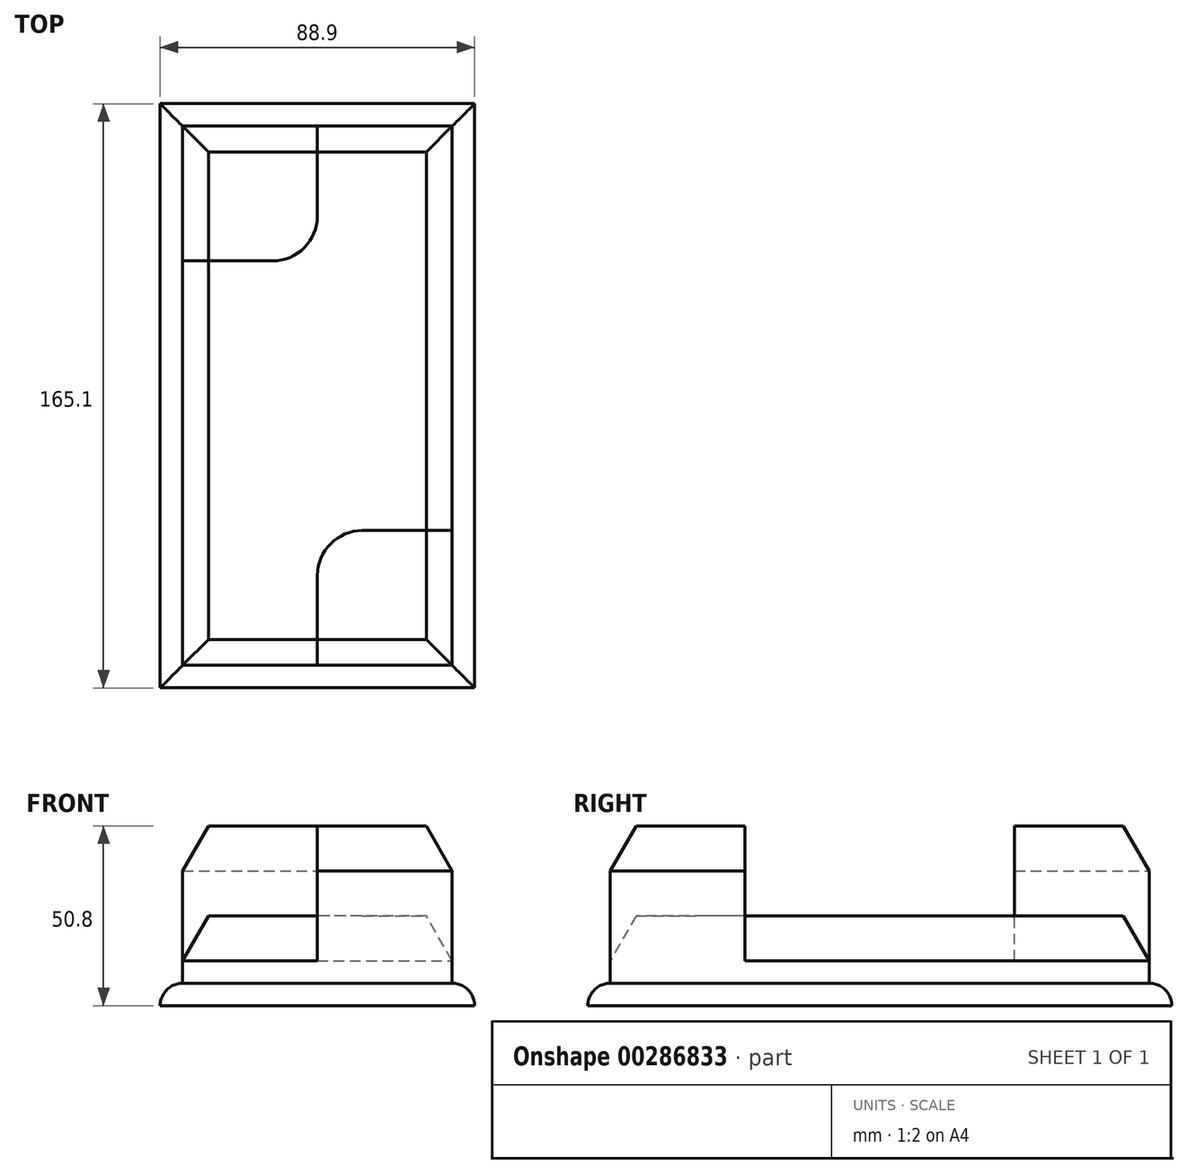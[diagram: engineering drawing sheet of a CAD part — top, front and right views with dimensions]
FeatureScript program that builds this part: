
annotation { "Feature Type Name" : "Feature", "Feature Type Description" : "" }
export const myFeature = defineFeature(function(context is Context, id is Id, definition is map)
    precondition{}
    {
        {
            var Q0;
            Q0=qCreatedBy(makeId("Top.planeOp"),FACE);
            var sketch = newSketch(context, id + "F0", { "sketchPlane" : qUnion([Q0])});
            skLineSegment(sketch, "E0", {"start": v(-43.8, 68.26) * mm, "end": v(-43.8, -84.14) * mm});
            skLineSegment(sketch, "E1", {"start": v(-43.8, -84.14) * mm, "end": v(32.4, -84.14) * mm});
            skLineSegment(sketch, "E2", {"start": v(32.4, -84.14) * mm, "end": v(32.4, 68.26) * mm});
            skLineSegment(sketch, "E3", {"start": v(32.4, 68.26) * mm, "end": v(-43.8, 68.26) * mm});
            skLineSegment(sketch, "E4", {"start": v(-5.7, 68.26) * mm, "end": v(-5.7, 42.86) * mm});
            skLineSegment(sketch, "E5", {"start": v(-18.4, 30.16) * mm, "end": v(-43.8, 30.16) * mm});
            skPoint(sketch, "E6.visualSharp", {"position": v(-5.7, 30.16) * mm});
            skArc(sketch, "E6.filletArc", {"start": v(-18.4, 30.16) * mm, "mid": v(-9.43, 33.88) * mm, "end": v(-5.7, 42.86) * mm});
            skLineSegment(sketch, "E7.0", {"start": v(38.74, 74.61) * mm, "end": v(-50.16, 74.61) * mm});
            skLineSegment(sketch, "E7.1", {"start": v(38.74, -90.49) * mm, "end": v(38.74, 74.61) * mm});
            skLineSegment(sketch, "E7.2", {"start": v(-50.16, -90.49) * mm, "end": v(38.74, -90.49) * mm});
            skLineSegment(sketch, "E7.3", {"start": v(-50.16, 74.61) * mm, "end": v(-50.16, -90.49) * mm});
            skLineSegment(sketch, "E8", {"start": v(-5.7, -84.14) * mm, "end": v(-5.7, -58.74) * mm});
            skLineSegment(sketch, "E9", {"start": v(7, -46.04) * mm, "end": v(32.4, -46.04) * mm});
            skPoint(sketch, "E10.visualSharp", {"position": v(-5.7, -46.04) * mm});
            skArc(sketch, "E10.filletArc", {"start": v(7, -46.04) * mm, "mid": v(-1.99, -49.76) * mm, "end": v(-5.7, -58.74) * mm});
            skSolve(sketch);
        }
        {
            var Q0;
            Q0=qSketchRegion(id+"F0",true);
            extrude(context, id + "F1", {"entities" : qUnion([Q0]), "depth" : 6.35 * mm});
        }
        {
            var Q0;
            {var subQ8=sQuery(id+"F0.wireOp",EDGE,"E4");Q0=makeQuery(id+"F0.imprint","IMPRINT",FACE,{"disambiguationData":[TD([[makeQuery(id+"F0.imprint","IMPRINT",EDGE,{"derivedFrom":subQ8}),1.0]])]});}
            extrude(context, id + "F2", {"entities" : qUnion([Q0]), "operationType" : NewBodyOperationType.ADD, "depth" : 25.4 * mm});
        }
        {
            var Q0;
            {var subQ1=sQuery(id+"F0.wireOp",EDGE,"E4");Q0=makeQuery(id+"F0.imprint","IMPRINT",FACE,{"disambiguationData":[TD([[makeQuery(id+"F0.imprint","IMPRINT",EDGE,{"derivedFrom":subQ1}),-1.0]])]});}
            var Q1;
            {var subQ1=sQuery(id+"F0.wireOp",EDGE,"E8");Q1=makeQuery(id+"F0.imprint","IMPRINT",FACE,{"disambiguationData":[TD([[makeQuery(id+"F0.imprint","IMPRINT",EDGE,{"derivedFrom":subQ1}),-1.0]])]});}
            extrude(context, id + "F3", {"entities" : qUnion([Q0, Q1]), "operationType" : NewBodyOperationType.ADD, "depth" : 50.8 * mm});
        }
        {
            var Q0;
            Q0=makeQuery(id+"F2.opExtrude","CAP_EDGE",EDGE,{"disambiguationData":[OSD([sQuery(id+"F0.wireOp",EDGE,"E1")])],"isStart":false});
            var Q1;
            Q1=makeQuery(id+"F3.opExtrude","CAP_EDGE",EDGE,{"disambiguationData":[OSD([sQuery(id+"F0.wireOp",EDGE,"E1")])],"isStart":false});
            var Q2;
            Q2=makeQuery(id+"F3.opExtrude","CAP_EDGE",EDGE,{"disambiguationData":[OSD([sQuery(id+"F0.wireOp",EDGE,"E2")])],"isStart":false});
            var Q3;
            Q3=makeQuery(id+"F2.opExtrude","CAP_EDGE",EDGE,{"disambiguationData":[OSD([sQuery(id+"F0.wireOp",EDGE,"E2")])],"isStart":false});
            var Q4;
            Q4=makeQuery(id+"F2.opExtrude","CAP_EDGE",EDGE,{"disambiguationData":[OSD([sQuery(id+"F0.wireOp",EDGE,"E3")])],"isStart":false});
            var Q5;
            Q5=makeQuery(id+"F3.opExtrude","CAP_EDGE",EDGE,{"disambiguationData":[OSD([sQuery(id+"F0.wireOp",EDGE,"E3")])],"isStart":false});
            var Q6;
            Q6=makeQuery(id+"F3.opExtrude","CAP_EDGE",EDGE,{"disambiguationData":[OSD([sQuery(id+"F0.wireOp",EDGE,"E0")])],"isStart":false});
            var Q7;
            Q7=makeQuery(id+"F2.opExtrude","CAP_EDGE",EDGE,{"disambiguationData":[OSD([sQuery(id+"F0.wireOp",EDGE,"E0")])],"isStart":false});
            chamfer(context, id + "F4", {"entities" : qUnion([Q0, Q1, Q2, Q3, Q4, Q5, Q6, Q7]), "chamferType" : ChamferType.OFFSET_ANGLE, "width" : 12.7 * mm, "oppositeDirection" : true, "angle" : 30 * degree, "tangentPropagation" : true});
        }
        {
            var Q0;
            Q0=makeQuery(id+"F1.opExtrude","CAP_EDGE",EDGE,{"disambiguationData":[OSD([sQuery(id+"F0.wireOp",EDGE,"E7.1")])],"isStart":false});
            var Q1;
            Q1=makeQuery(id+"F1.opExtrude","CAP_EDGE",EDGE,{"disambiguationData":[OSD([sQuery(id+"F0.wireOp",EDGE,"E7.0")])],"isStart":false});
            var Q2;
            Q2=makeQuery(id+"F1.opExtrude","CAP_EDGE",EDGE,{"disambiguationData":[OSD([sQuery(id+"F0.wireOp",EDGE,"E7.3")])],"isStart":false});
            var Q3;
            Q3=makeQuery(id+"F1.opExtrude","CAP_EDGE",EDGE,{"disambiguationData":[OSD([sQuery(id+"F0.wireOp",EDGE,"E7.2")])],"isStart":false});
            fillet(context, id + "F5", {"entities" : qUnion([Q0, Q1, Q2, Q3]), "radius" : 6.35 * mm, "tangentPropagation" : true, "allowEdgeOverflow" : false});
        }
    });
